# Revit family: CONTURA II 530 AC BASIN NTH NOF
name_source: partatom
category: Plumbing Fixtures
units: mm (PartAtom-declared; Revit-internal decimal feet)

## family parameters
Cut with Voids When Loaded = Yes
Host = Face
OmniClass Number = 23.45.05.14.14
OmniClass Title = Sinks/Lavatories
Part Type = Normal
Room Calculation Point = No
Round Connector Dimension = Use Diameter
Shared = No

## types (3) — shared parameters
Assembly Code = D2010400
CW Connection = No
HW Connection = No
Manufacturer = GWA Bathrooms & Kitchens
Material_Waste = GWA-Metalwork-White
URL = https://www.caroma.com.au
Vent Connection = No
Waste Connection = Yes
zero-valued in all types: Default Elevation

## per-type parameters (varying)
| type | Material_Basin | Model |
| CONTURA II 530 AC BASIN NTH NOF - WHITE | GWA-Porcelain-White | 853200W |
| CONTURA II 530 AC BASIN NTH NOF - MATTE CLAY | GWA-Porcelain-Matte-Clay | 853200CL |
| CONTURA II 530 AC BASIN NTH NOF - MATTE WHITE | GWA-Porcelain-Matte-White | 853200MW |

note: column(s) folded — value = type name in every type: Description

## geometry (parser evidence)
native form markers: Sweep x2
no freeform markers — native parametric forms only
